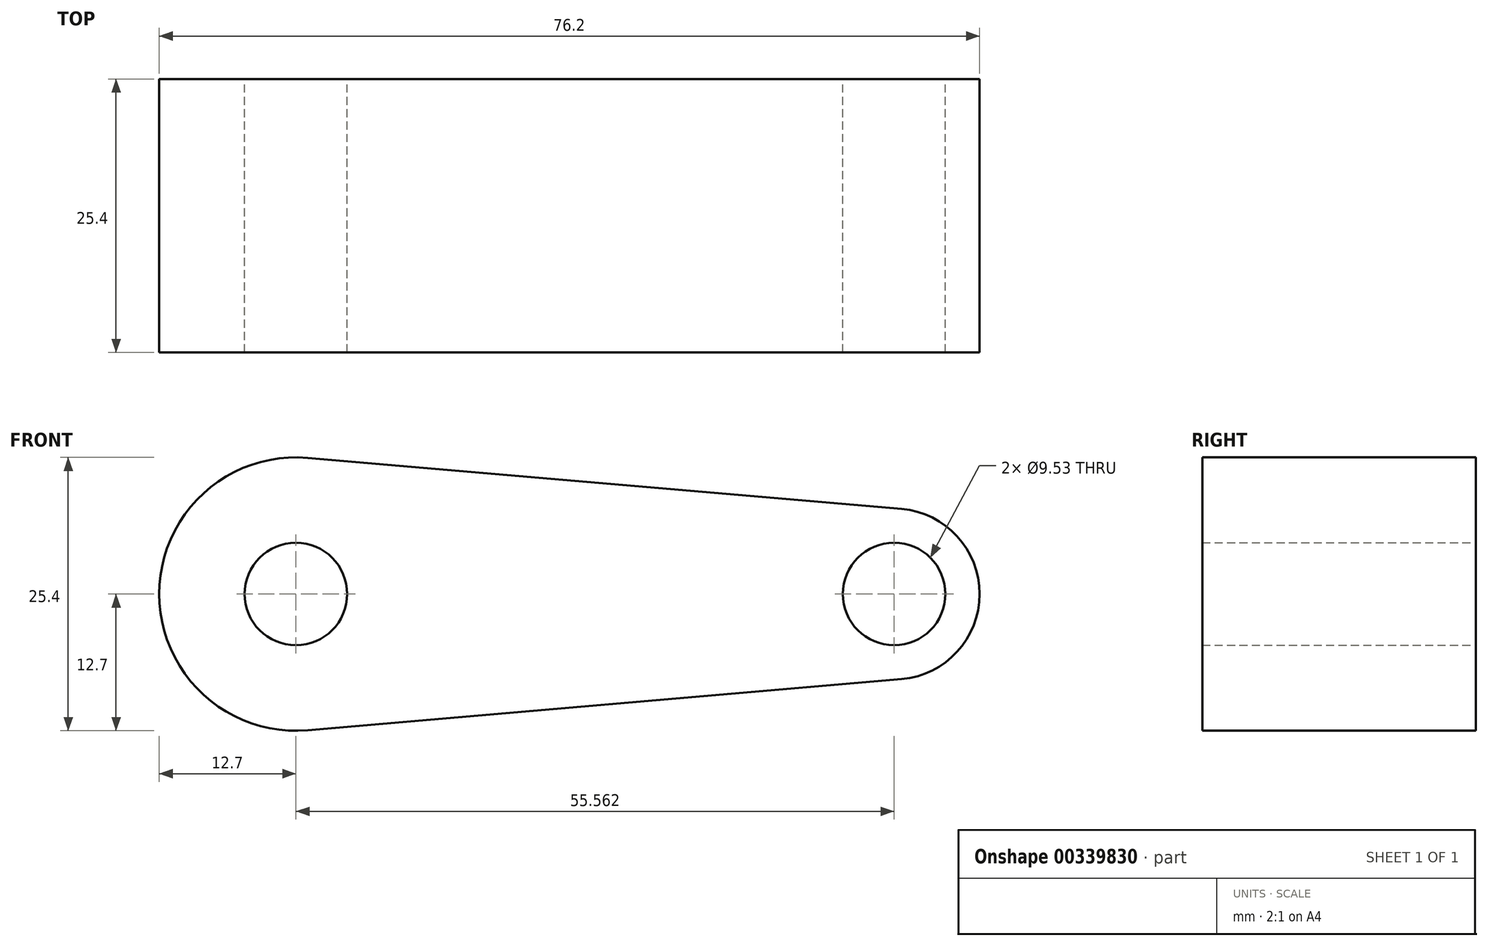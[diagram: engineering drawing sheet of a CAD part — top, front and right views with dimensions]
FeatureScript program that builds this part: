
annotation { "Feature Type Name" : "Feature", "Feature Type Description" : "" }
export const myFeature = defineFeature(function(context is Context, id is Id, definition is map)
    precondition{}
    {
        {
            var Q0;
            Q0=qCreatedBy(makeId("Front.planeOp"),FACE);
            var sketch = newSketch(context, id + "F0", { "sketchPlane" : qUnion([Q0])});
            skCircle(sketch, "E0", {"center": v(0, 0) * mm, "radius": 12.7 * mm});
            skCircle(sketch, "E1", {"center": v(55.56, 0) * mm, "radius": 7.94 * mm});
            skLineSegment(sketch, "E2", {"start": v(1.09, -12.65) * mm, "end": v(56.24, -7.9) * mm});
            skLineSegment(sketch, "E3", {"start": v(1.09, 12.65) * mm, "end": v(56.24, 7.9) * mm});
            skCircle(sketch, "E4", {"center": v(0, 0) * mm, "radius": 4.76 * mm});
            skCircle(sketch, "E5", {"center": v(55.56, 0) * mm, "radius": 4.76 * mm});
            skSolve(sketch);
        }
        {
            var Q0;
            Q0 = qSketchRegion(id + "F0", true);
            extrude(context, id + "F1", {"entities" : qUnion([Q0]), "depth" : 25.4 * mm});
        }
        {
            var Q0;
            Q0 = qSketchRegion(id + "F0", true);
            extrude(context, id + "F2", {"entities" : qUnion([Q0]), "operationType" : NewBodyOperationType.ADD, "depth" : 25.4 * mm});
        }
    });
